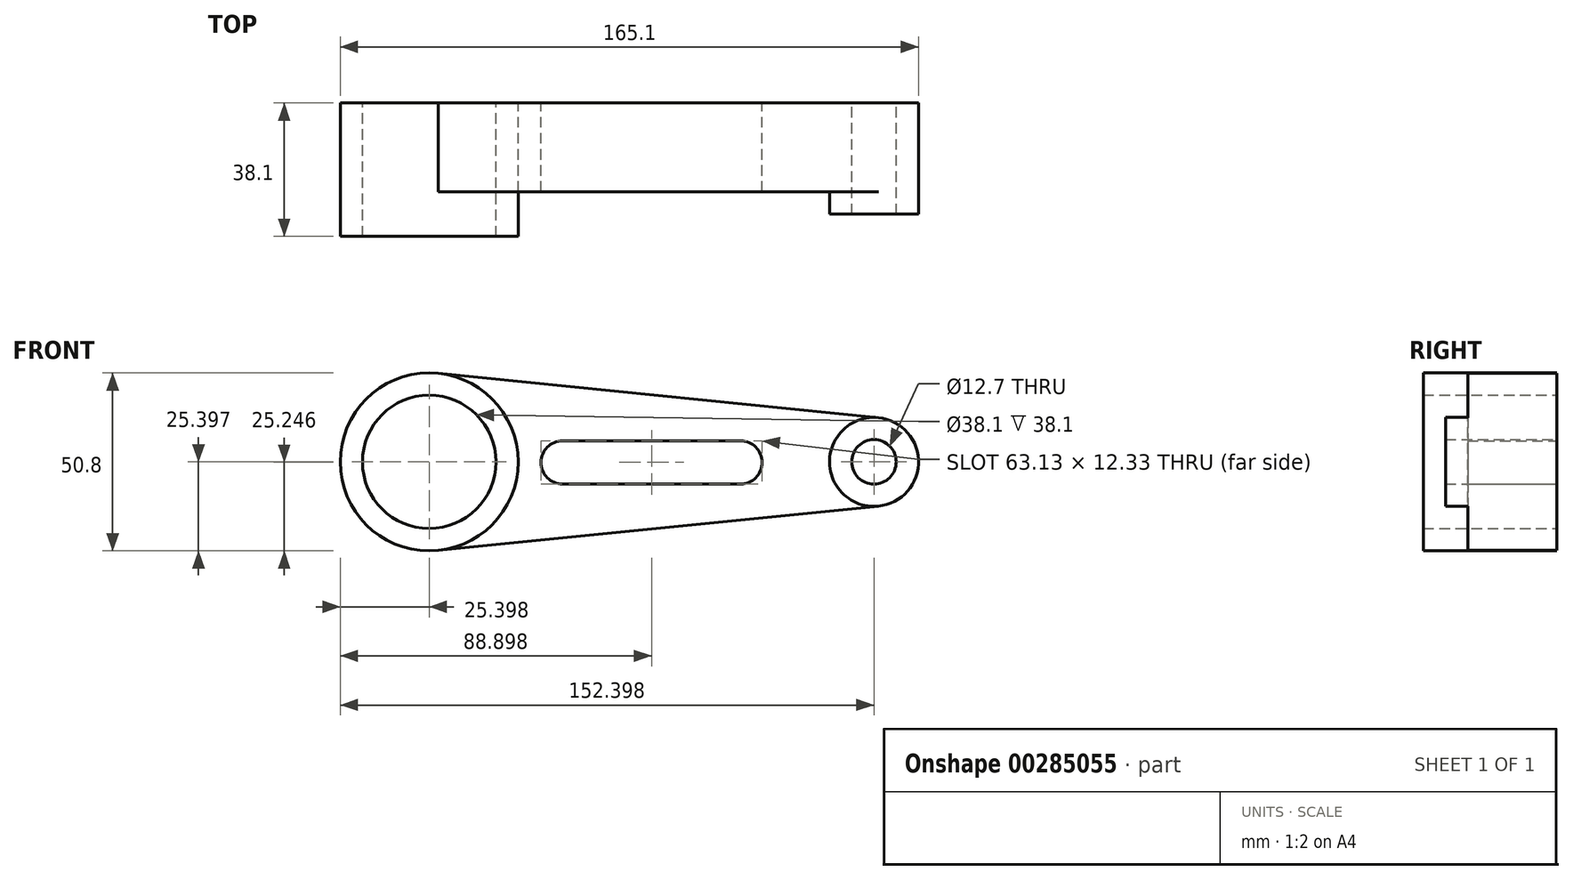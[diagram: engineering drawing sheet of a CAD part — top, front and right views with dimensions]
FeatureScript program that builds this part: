
annotation { "Feature Type Name" : "Feature", "Feature Type Description" : "" }
export const myFeature = defineFeature(function(context is Context, id is Id, definition is map)
    precondition{}
    {
        {
            var Q0;
            Q0=qCreatedBy(makeId("Front.planeOp"),FACE);
            var sketch = newSketch(context, id + "F0", { "sketchPlane" : qUnion([Q0])});
            skCircle(sketch, "E0", {"center": v(-65.47, 21.66) * mm, "radius": 25.4 * mm});
            skCircle(sketch, "E1", {"center": v(-65.47, 21.66) * mm, "radius": 19.05 * mm});
            skCircle(sketch, "E2", {"center": v(61.53, 21.66) * mm, "radius": 12.7 * mm});
            skCircle(sketch, "E3", {"center": v(61.53, 21.66) * mm, "radius": 6.35 * mm});
            skLineSegment(sketch, "E4", {"start": v(-62.93, 46.93) * mm, "end": v(62.8, 34.3) * mm});
            skLineSegment(sketch, "E5", {"start": v(-62.93, -3.62) * mm, "end": v(62.8, 9.02) * mm});
            skLineSegment(sketch, "E6.bottom", {"start": v(-27.37, 27.67) * mm, "end": v(23.43, 27.67) * mm});
            skLineSegment(sketch, "E6.top", {"start": v(-27.37, 15.34) * mm, "end": v(23.43, 15.34) * mm});
            skLineSegment(sketch, "E6.left", {"start": v(-27.37, 21.66) * mm, "end": v(-27.37, 21.5) * mm});
            skLineSegment(sketch, "E6.right", {"start": v(23.43, 21.66) * mm, "end": v(23.43, 21.5) * mm});
            skArc(sketch, "E7", {"start": v(-27.37, 27.67) * mm, "mid": v(-33.54, 21.5) * mm, "end": v(-27.37, 15.34) * mm});
            skArc(sketch, "E8", {"start": v(23.43, 15.34) * mm, "mid": v(29.6, 21.5) * mm, "end": v(23.43, 27.67) * mm});
            skSolve(sketch);
        }
        {
            var Q0;
            Q0=makeQuery(id+"F0.imprint","IMPRINT",FACE,{"disambiguationData":[TD([[makeQuery(id+"F0.imprint","IMPRINT",EDGE,{"derivedFrom":sQuery(id+"F0.wireOp",EDGE,"E1")}),-1.0]])]});
            extrude(context, id + "F1", {"entities" : qUnion([Q0]), "depth" : 38.1 * mm});
        }
        {
            var Q0;
            {var subQ1=sQuery(id+"F0.wireOp",EDGE,"E4");Q0=makeQuery(id+"F0.imprint","IMPRINT",FACE,{"disambiguationData":[TD([[makeQuery(id+"F0.imprint","IMPRINT",EDGE,{"derivedFrom":subQ1}),-1.0]])]});}
            extrude(context, id + "F2", {"entities" : qUnion([Q0]), "depth" : 25.4 * mm});
        }
        {
            var Q0;
            Q0=makeQuery(id+"F0.imprint","IMPRINT",FACE,{"disambiguationData":[TD([[makeQuery(id+"F0.imprint","IMPRINT",EDGE,{"derivedFrom":sQuery(id+"F0.wireOp",EDGE,"E3")}),-1.0]])]});
            extrude(context, id + "F3", {"entities" : qUnion([Q0]), "operationType" : NewBodyOperationType.ADD, "depth" : 31.75 * mm});
        }
    });
